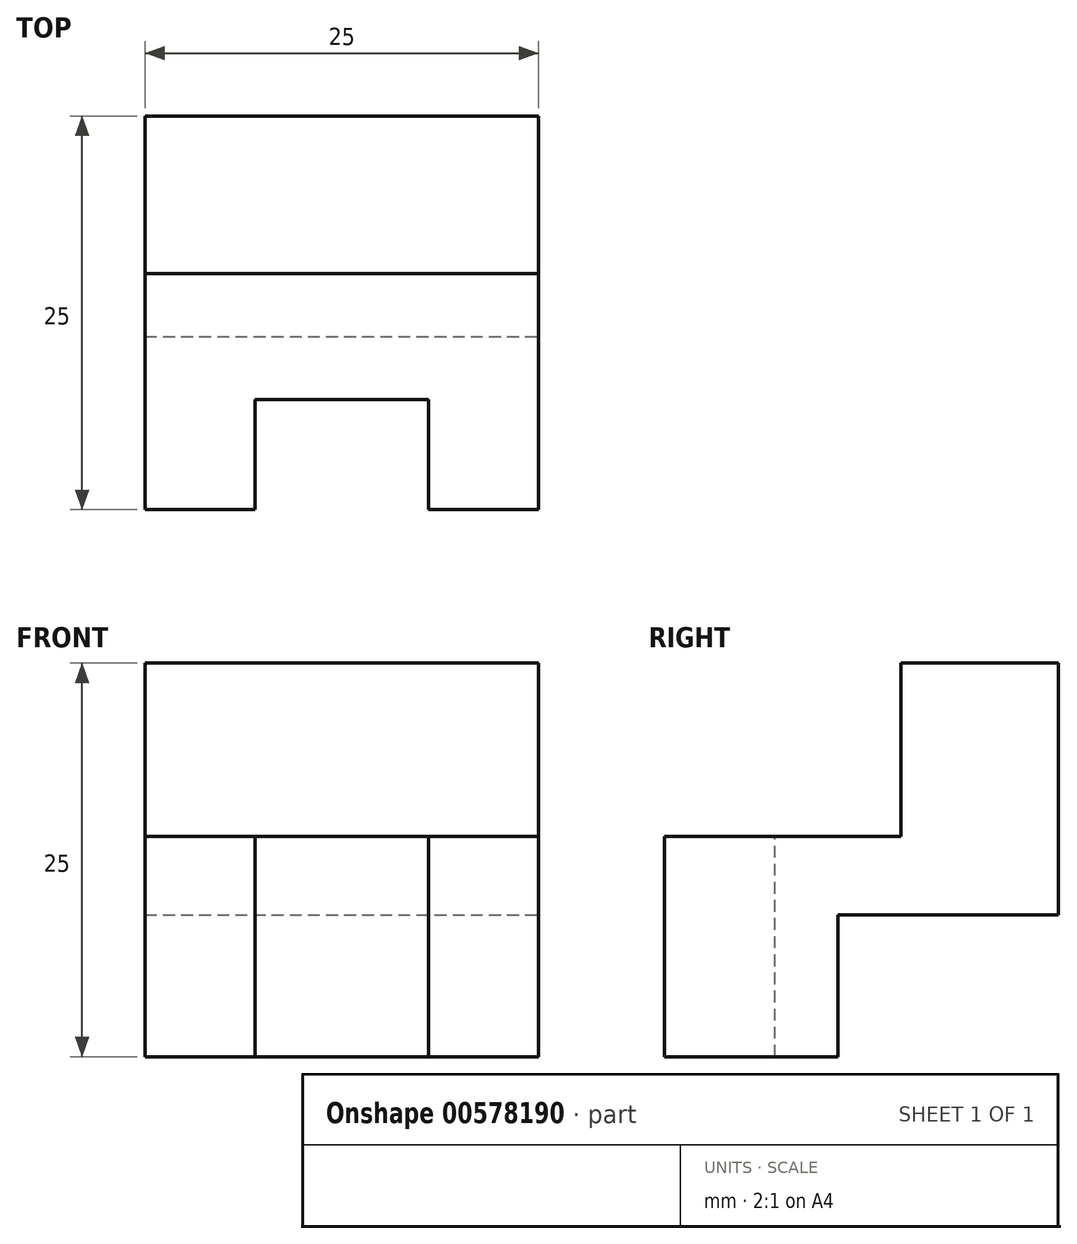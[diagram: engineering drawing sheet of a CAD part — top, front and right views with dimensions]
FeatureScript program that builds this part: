
annotation { "Feature Type Name" : "Feature", "Feature Type Description" : "" }
export const myFeature = defineFeature(function(context is Context, id is Id, definition is map)
    precondition{}
    {
        {
            var Q0;
            Q0=qCreatedBy(makeId("Right.planeOp"),FACE);
            var sketch = newSketch(context, id + "F0", { "sketchPlane" : qUnion([Q0])});
            skLineSegment(sketch, "E0", {"start": v(-11, 0) * mm, "end": v(0, 0) * mm});
            skLineSegment(sketch, "E1", {"start": v(0, 0) * mm, "end": v(0, 9) * mm});
            skLineSegment(sketch, "E2", {"start": v(0, 9) * mm, "end": v(14, 9) * mm});
            skLineSegment(sketch, "E3", {"start": v(14, 9) * mm, "end": v(14, 25) * mm});
            skLineSegment(sketch, "E4", {"start": v(14, 25) * mm, "end": v(4, 25) * mm});
            skLineSegment(sketch, "E5", {"start": v(4, 25) * mm, "end": v(4, 14) * mm});
            skLineSegment(sketch, "E6", {"start": v(4, 14) * mm, "end": v(-11, 14) * mm});
            skLineSegment(sketch, "E7", {"start": v(-11, 14) * mm, "end": v(-11, 0) * mm});
            skSolve(sketch);
        }
        {
            var Q0;
            Q0=makeQuery(id+"F0.imprint","IMPRINT",FACE,{"disambiguationData":[TD([[makeQuery(id+"F0.imprint","IMPRINT",EDGE,{"derivedFrom":sQuery(id+"F0.wireOp",EDGE,"E0")}),1.0]])]});
            extrude(context, id + "F1", {"entities" : qUnion([Q0]), "endBound" : BoundingType.SYMMETRIC, "oppositeDirection" : true, "depth" : 25 * mm, "offsetDistance" : 25 * mm});
        }
        {
            var Q0;
            Q0=makeQuery(id+"F1.opExtrude","SWEPT_FACE",FACE,{"disambiguationData":[OSD([sQuery(id+"F0.wireOp",EDGE,"E6")])]});
            var sketch = newSketch(context, id + "F2", { "sketchPlane" : qUnion([Q0])});
            skLineSegment(sketch, "E8", {"start": v(-5.5, -11) * mm, "end": v(-5.5, -4) * mm});
            skLineSegment(sketch, "E9", {"start": v(-5.5, -4) * mm, "end": v(5.5, -4) * mm});
            skLineSegment(sketch, "E10", {"start": v(5.5, -4) * mm, "end": v(5.5, -11) * mm});
            skSolve(sketch);
        }
        {
            var Q0;
            {var subQ0=sQuery(id+"F2.wireOp",EDGE,"E8");Q0=makeQuery(id+"F2.imprint","IMPRINT",FACE,{"disambiguationData":[TD([[makeQuery(id+"F2.imprint","IMPRINT",EDGE,{"derivedFrom":subQ0}),-1.0]])]});}
            extrude(context, id + "F3", {"entities" : qUnion([Q0]), "operationType" : NewBodyOperationType.REMOVE, "endBound" : BoundingType.THROUGH_ALL, "oppositeDirection" : true, "depth" : 25 * mm, "offsetDistance" : 25 * mm});
        }
    });
